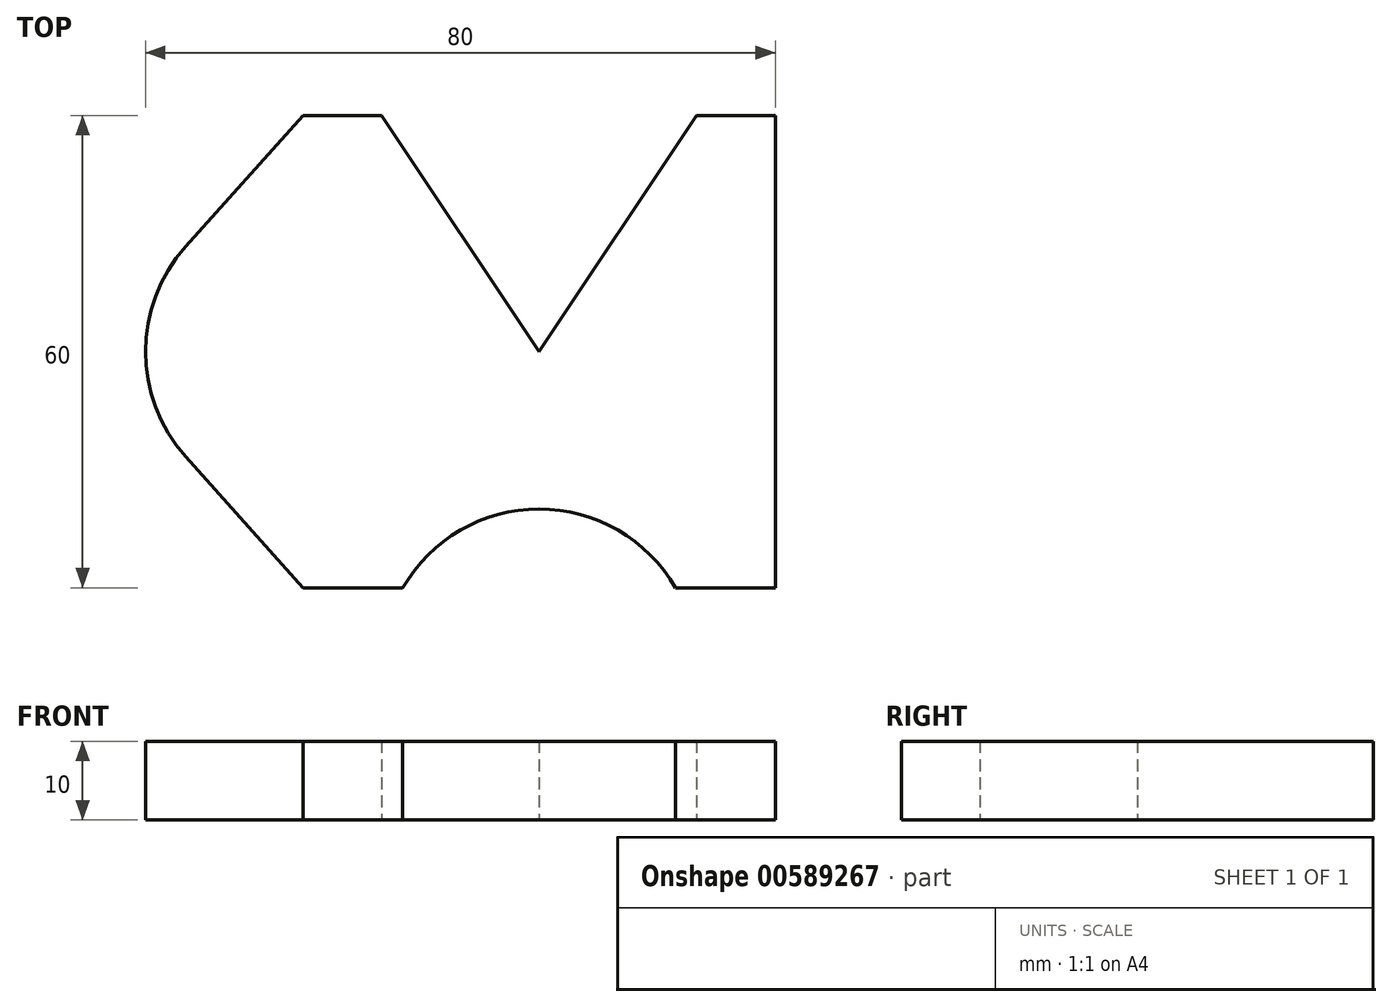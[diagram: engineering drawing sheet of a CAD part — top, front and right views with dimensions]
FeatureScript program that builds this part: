
annotation { "Feature Type Name" : "Feature", "Feature Type Description" : "" }
export const myFeature = defineFeature(function(context is Context, id is Id, definition is map)
    precondition{}
    {
        {
            var Q0;
            Q0=qCreatedBy(makeId("Top.planeOp"),FACE);
            var sketch = newSketch(context, id + "F0", { "sketchPlane" : qUnion([Q0])});
            skLineSegment(sketch, "E0", {"start": v(0, 0) * mm, "end": v(20, 30) * mm});
            skLineSegment(sketch, "E1", {"start": v(20, 30) * mm, "end": v(30, 30) * mm});
            skLineSegment(sketch, "E2", {"start": v(30, 30) * mm, "end": v(30, -30) * mm});
            skLineSegment(sketch, "E3", {"start": v(30, -30) * mm, "end": v(17.32, -30) * mm});
            skLineSegment(sketch, "E4", {"start": v(-17.32, -30) * mm, "end": v(-30, -30) * mm});
            skLineSegment(sketch, "E5", {"start": v(-30, -30) * mm, "end": v(-44.9, -13.33) * mm});
            skLineSegment(sketch, "E6", {"start": v(0, 0) * mm, "end": v(-20, 30) * mm});
            skLineSegment(sketch, "E7", {"start": v(-20, 30) * mm, "end": v(-30, 30) * mm});
            skLineSegment(sketch, "E8", {"start": v(-30, 30) * mm, "end": v(-44.9, 13.33) * mm});
            skArc(sketch, "E9", {"start": v(-44.9, 13.33) * mm, "mid": v(-50, 0) * mm, "end": v(-44.9, -13.33) * mm});
            skArc(sketch, "E10", {"start": v(17.32, -30) * mm, "mid": v(0, -20) * mm, "end": v(-17.32, -30) * mm});
            skLineSegment(sketch, "E11", {"start": v(-30, 30) * mm, "end": v(-30, -40.54) * mm, "construction": true});
            skSolve(sketch);
        }
        {
            var Q0;
            Q0=makeQuery(id+"F0.imprint","IMPRINT",FACE,{"disambiguationData":[TD([[makeQuery(id+"F0.imprint","IMPRINT",EDGE,{"derivedFrom":sQuery(id+"F0.wireOp",EDGE,"E0")}),-1.0]])]});
            extrude(context, id + "F1", {"entities" : qUnion([Q0]), "depth" : 10 * mm, "offsetDistance" : 25 * mm});
        }
    });
